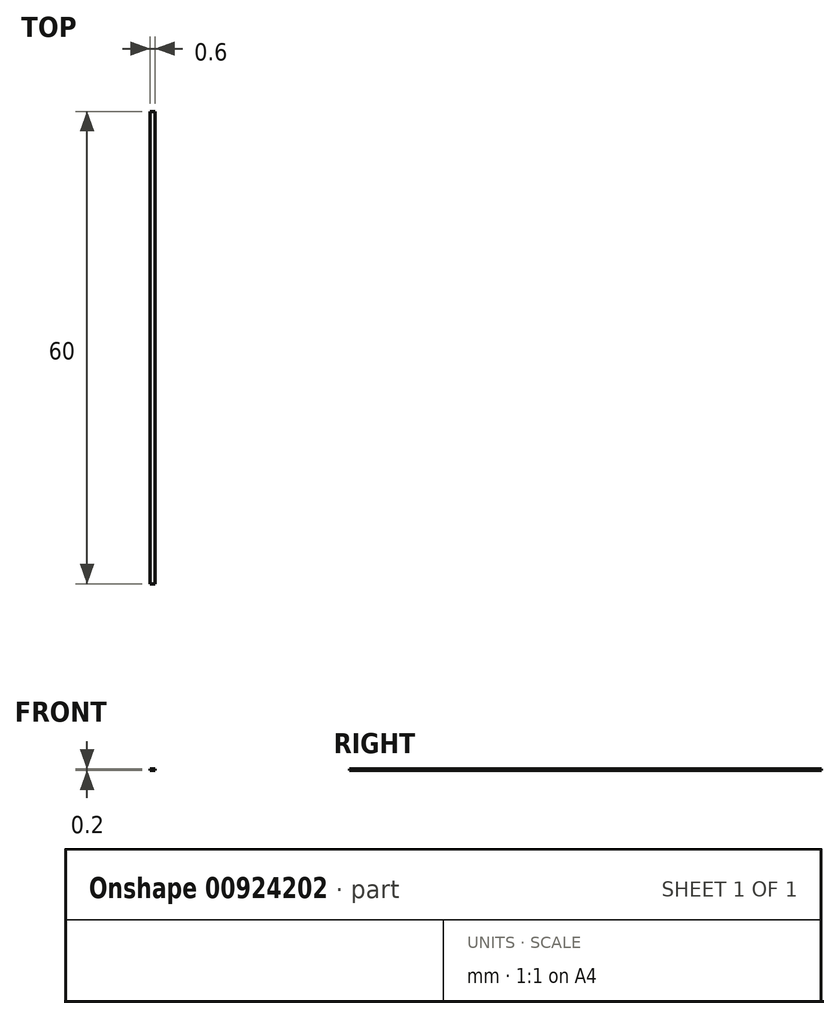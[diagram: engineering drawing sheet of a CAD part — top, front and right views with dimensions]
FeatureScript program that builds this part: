
annotation { "Feature Type Name" : "Feature", "Feature Type Description" : "" }
export const myFeature = defineFeature(function(context is Context, id is Id, definition is map)
    precondition{}
    {
        {
            var Q0;
            Q0=qCreatedBy(makeId("Top.planeOp"),FACE);
            var sketch = newSketch(context, id + "F0", { "sketchPlane" : qUnion([Q0])});
            skLineSegment(sketch, "E0", {"start": v(0, 0) * mm, "end": v(-0.6, 0) * mm});
            skLineSegment(sketch, "E1", {"start": v(-0.6, 0) * mm, "end": v(-0.6, -60) * mm});
            skLineSegment(sketch, "E2", {"start": v(-0.6, -60) * mm, "end": v(0, -60) * mm});
            skLineSegment(sketch, "E3", {"start": v(0, -60) * mm, "end": v(0, 0) * mm});
            skSolve(sketch);
        }
        {
            var Q0;
            Q0 = qSketchRegion(id + "F0", true);
            extrude(context, id + "F1", {"entities" : qUnion([Q0]), "depth" : 0.1 * mm, "offsetDistance" : 25 * mm});
        }
        {
            var Q0;
            Q0 = qSketchRegion(id + "FzQwHhmsBeE5nHo_1", true);
            var Q1;
            Q1=makeQuery(id+"F1.opExtrude","CAP_FACE",FACE,{"disambiguationData":[OSD([sQuery(id+"F0.wireOp",EDGE,"E0"),sQuery(id+"F0.wireOp",EDGE,"E1"),sQuery(id+"F0.wireOp",EDGE,"E2"),sQuery(id+"F0.wireOp",EDGE,"E3")])],"isStart":false});
            extrude(context, id + "F2", {"entities" : qUnion([Q0, Q1]), "operationType" : NewBodyOperationType.ADD, "depth" : 0.1 * mm, "offsetDistance" : 25 * mm});
        }
    });
